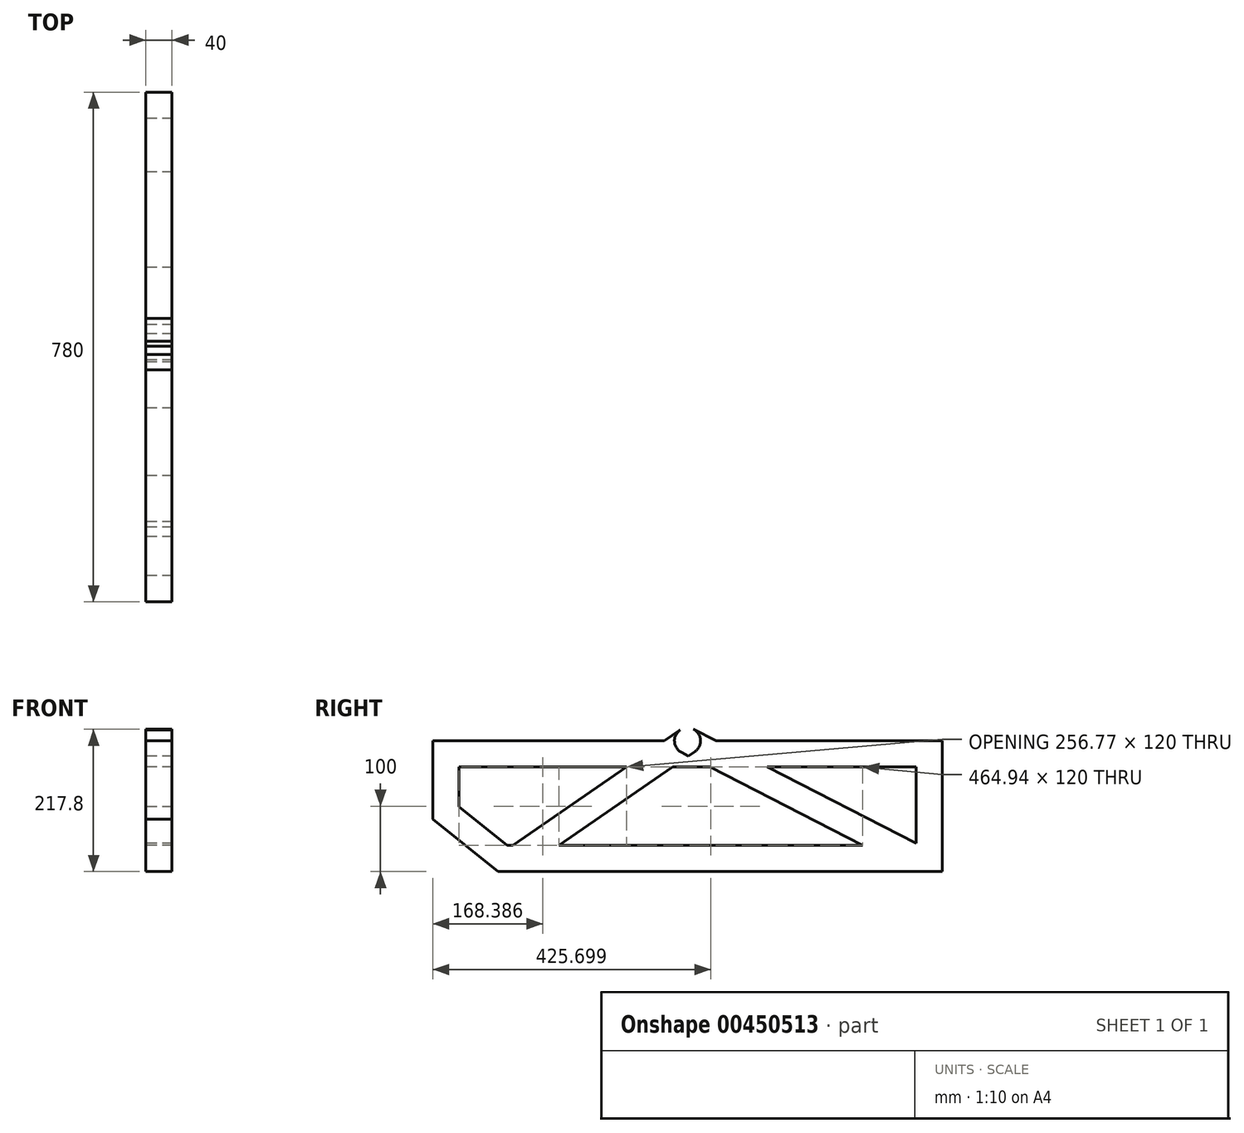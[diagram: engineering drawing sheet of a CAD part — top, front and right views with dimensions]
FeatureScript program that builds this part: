
annotation { "Feature Type Name" : "Feature", "Feature Type Description" : "" }
export const myFeature = defineFeature(function(context is Context, id is Id, definition is map)
    precondition{}
    {
        {
            var Q0;
            Q0=qCreatedBy(makeId("Right.planeOp"),FACE);
            var sketch = newSketch(context, id + "F0", { "sketchPlane" : qUnion([Q0])});
            skLineSegment(sketch, "E0", {"start": v(-369, 0) * mm, "end": v(-369, -20) * mm});
            skLineSegment(sketch, "E1", {"start": v(-369, -20) * mm, "end": v(-369, -100) * mm});
            skLineSegment(sketch, "E2", {"start": v(-369, -20) * mm, "end": v(-269, -20) * mm});
            skLineSegment(sketch, "E3", {"start": v(-369, -20) * mm, "end": v(-269, -100) * mm});
            skLineSegment(sketch, "E4", {"start": v(-269, -100) * mm, "end": v(411, -100) * mm});
            skLineSegment(sketch, "E5", {"start": v(411, -100) * mm, "end": v(411, 100) * mm});
            skLineSegment(sketch, "E6", {"start": v(411, 100) * mm, "end": v(-369, 100) * mm});
            skLineSegment(sketch, "E7", {"start": v(-369, 100) * mm, "end": v(-369, 0) * mm});
            skLineSegment(sketch, "E8", {"start": v(-269, -100) * mm, "end": v(21, 100) * mm});
            skLineSegment(sketch, "E9", {"start": v(21, 100) * mm, "end": v(411, -100) * mm});
            skLineSegment(sketch, "E10.0", {"start": v(-329, -0.78) * mm, "end": v(-254.97, -60) * mm});
            skLineSegment(sketch, "E10.1", {"start": v(-329, 60) * mm, "end": v(-329, -0.78) * mm});
            skLineSegment(sketch, "E10.2", {"start": v(-254.97, -60) * mm, "end": v(371, -60) * mm});
            skLineSegment(sketch, "E10.3", {"start": v(371, -60) * mm, "end": v(371, 60) * mm});
            skLineSegment(sketch, "E10.4", {"start": v(371, 60) * mm, "end": v(-329, 60) * mm});
            skArc(sketch, "E11.0.startCap", {"start": v(-257.65, -116.46) * mm, "mid": v(-285.46, -111.35) * mm, "end": v(-280.35, -83.54) * mm});
            skArc(sketch, "E11.0.endCap", {"start": v(9.65, 116.46) * mm, "mid": v(37.46, 111.35) * mm, "end": v(32.35, 83.54) * mm});
            skLineSegment(sketch, "E11.0.left", {"start": v(-280.35, -83.54) * mm, "end": v(9.65, 116.46) * mm});
            skLineSegment(sketch, "E11.0.right", {"start": v(-257.65, -116.46) * mm, "end": v(32.35, 83.54) * mm});
            skArc(sketch, "E11.1.startCap", {"start": v(11.87, 82.2) * mm, "mid": v(3.2, 109.13) * mm, "end": v(30.13, 117.8) * mm});
            skArc(sketch, "E11.1.endCap", {"start": v(420.13, -82.2) * mm, "mid": v(428.8, -109.13) * mm, "end": v(401.87, -117.8) * mm});
            skLineSegment(sketch, "E11.1.left", {"start": v(30.13, 117.8) * mm, "end": v(420.13, -82.2) * mm});
            skLineSegment(sketch, "E11.1.right", {"start": v(11.87, 82.2) * mm, "end": v(401.87, -117.8) * mm});
            skSolve(sketch);
        }
        {
            var Q0;
            {var subQ0=sQuery(id+"F0.wireOp",EDGE,"E10.2");var subQ1=sQuery(id+"F0.wireOp",EDGE,"E10.0");var subQ2=makeQuery(id+"F0.imprint","INTERSECT",VERTEX,{"derivedFrom":[subQ1,subQ0]});Q0=makeQuery(id+"F0.imprint","IMPRINT",FACE,{"disambiguationData":[TD([[makeQuery(id+"F0.imprint","IMPRINT",EDGE,{"disambiguationData":[TD([[subQ2,1.0]])],"derivedFrom":subQ1}),-1.0]])]});}
            var Q1;
            {var subQ0=sQuery(id+"F0.wireOp",EDGE,"E11.0.right");var subQ1=sQuery(id+"F0.wireOp",EDGE,"E4");var subQ2=makeQuery(id+"F0.imprint","INTERSECT",VERTEX,{"derivedFrom":[subQ1,subQ0]});Q1=makeQuery(id+"F0.imprint","IMPRINT",FACE,{"disambiguationData":[TD([[makeQuery(id+"F0.imprint","IMPRINT",EDGE,{"disambiguationData":[TD([[subQ2,-1.0]])],"derivedFrom":subQ1}),1.0]])]});}
            var Q2;
            {var subQ6=sQuery(id+"F0.wireOp",EDGE,"E6");var subQ7=sQuery(id+"F0.wireOp",EDGE,"E5");var subQ8=makeQuery(id+"F0.imprint","INTERSECT",VERTEX,{"derivedFrom":[subQ7,subQ6]});Q2=makeQuery(id+"F0.imprint","IMPRINT",FACE,{"disambiguationData":[TD([[makeQuery(id+"F0.imprint","IMPRINT",EDGE,{"disambiguationData":[TD([[subQ8,1.0]])],"derivedFrom":subQ7}),1.0]])]});}
            var Q3;
            {var subQ3=sQuery(id+"F0.wireOp",EDGE,"E11.1.left");var subQ7=sQuery(id+"F0.wireOp",EDGE,"E6");var subQ8=makeQuery(id+"F0.imprint","INTERSECT",VERTEX,{"derivedFrom":[subQ7,subQ3]});Q3=makeQuery(id+"F0.imprint","IMPRINT",FACE,{"disambiguationData":[TD([[makeQuery(id+"F0.imprint","IMPRINT",EDGE,{"disambiguationData":[TD([[subQ8,-1.0]])],"derivedFrom":subQ7}),1.0]])]});}
            var Q4;
            {var subQ1=sQuery(id+"F0.wireOp",EDGE,"E11.0.endCap");var subQ6=sQuery(id+"F0.wireOp",EDGE,"E9");var subQ9=makeQuery(id+"F0.imprint","INTERSECT",VERTEX,{"derivedFrom":[subQ6,subQ1]});Q4=makeQuery(id+"F0.imprint","IMPRINT",FACE,{"disambiguationData":[TD([[makeQuery(id+"F0.imprint","IMPRINT",EDGE,{"disambiguationData":[TD([[subQ9,-1.0]])],"derivedFrom":subQ6}),-1.0]])]});}
            var Q5;
            {var subQ0=sQuery(id+"F0.wireOp",EDGE,"E11.1.right");var subQ1=sQuery(id+"F0.wireOp",EDGE,"E10.4");var subQ2=makeQuery(id+"F0.imprint","INTERSECT",VERTEX,{"derivedFrom":[subQ1,subQ0]});Q5=makeQuery(id+"F0.imprint","IMPRINT",FACE,{"disambiguationData":[TD([[makeQuery(id+"F0.imprint","IMPRINT",EDGE,{"disambiguationData":[TD([[subQ2,-1.0]])],"derivedFrom":subQ1}),-1.0]])]});}
            var Q6;
            {var subQ3=sQuery(id+"F0.wireOp",EDGE,"E8");var subQ6=sQuery(id+"F0.wireOp",EDGE,"E10.4");var subQ9=makeQuery(id+"F0.imprint","INTERSECT",VERTEX,{"derivedFrom":[subQ3,subQ6]});Q6=makeQuery(id+"F0.imprint","IMPRINT",FACE,{"disambiguationData":[TD([[makeQuery(id+"F0.imprint","IMPRINT",EDGE,{"disambiguationData":[TD([[subQ9,-1.0]])],"derivedFrom":subQ3}),-1.0]])]});}
            var Q7;
            {var subQ0=sQuery(id+"F0.wireOp",EDGE,"E11.0.left");var subQ1=sQuery(id+"F0.wireOp",EDGE,"E6");var subQ2=makeQuery(id+"F0.imprint","INTERSECT",VERTEX,{"derivedFrom":[subQ1,subQ0]});Q7=makeQuery(id+"F0.imprint","IMPRINT",FACE,{"disambiguationData":[TD([[makeQuery(id+"F0.imprint","IMPRINT",EDGE,{"disambiguationData":[TD([[subQ2,1.0]])],"derivedFrom":subQ1}),1.0]])]});}
            var Q8;
            {var subQ1=sQuery(id+"F0.wireOp",EDGE,"E6");var subQ3=sQuery(id+"F0.wireOp",EDGE,"E11.1.startCap");var subQ4=makeQuery(id+"F0.imprint","INTERSECT",VERTEX,{"derivedFrom":[subQ1,subQ3]});Q8=makeQuery(id+"F0.imprint","IMPRINT",FACE,{"disambiguationData":[TD([[makeQuery(id+"F0.imprint","IMPRINT",EDGE,{"disambiguationData":[TD([[subQ4,1.0]])],"derivedFrom":subQ3}),-1.0]])]});}
            var Q9;
            {var subQ0=sQuery(id+"F0.wireOp",EDGE,"E11.0.right");var subQ1=sQuery(id+"F0.wireOp",EDGE,"E11.0.endCap");var subQ2=makeQuery(id+"F0.imprint","INTERSECT",VERTEX,{"derivedFrom":[subQ1,subQ0]});Q9=makeQuery(id+"F0.imprint","IMPRINT",FACE,{"disambiguationData":[TD([[makeQuery(id+"F0.imprint","IMPRINT",EDGE,{"disambiguationData":[TD([[subQ2,1.0]])],"derivedFrom":subQ1}),-1.0]])]});}
            var Q10;
            {var subQ1=sQuery(id+"F0.wireOp",EDGE,"E6");var subQ3=sQuery(id+"F0.wireOp",EDGE,"E11.0.endCap");var subQ4=makeQuery(id+"F0.imprint","INTERSECT",VERTEX,{"derivedFrom":[subQ1,subQ3]});Q10=makeQuery(id+"F0.imprint","IMPRINT",FACE,{"disambiguationData":[TD([[makeQuery(id+"F0.imprint","IMPRINT",EDGE,{"disambiguationData":[TD([[subQ4,-1.0]])],"derivedFrom":subQ3}),-1.0]])]});}
            var Q11;
            {var subQ5=sQuery(id+"F0.wireOp",EDGE,"E0");Q11=makeQuery(id+"F0.imprint","IMPRINT",FACE,{"disambiguationData":[TD([[makeQuery(id+"F0.imprint","IMPRINT",EDGE,{"derivedFrom":subQ5}),1.0]])]});}
            var Q12;
            {var subQ0=sQuery(id+"F0.wireOp",EDGE,"E8");var subQ5=sQuery(id+"F0.wireOp",EDGE,"E10.2");var subQ6=makeQuery(id+"F0.imprint","INTERSECT",VERTEX,{"derivedFrom":[subQ0,subQ5]});Q12=makeQuery(id+"F0.imprint","IMPRINT",FACE,{"disambiguationData":[TD([[makeQuery(id+"F0.imprint","IMPRINT",EDGE,{"disambiguationData":[TD([[subQ6,-1.0]])],"derivedFrom":subQ5}),-1.0]])]});}
            var Q13;
            {var subQ0=sQuery(id+"F0.wireOp",EDGE,"E8");var subQ3=sQuery(id+"F0.wireOp",EDGE,"E10.2");var subQ4=makeQuery(id+"F0.imprint","INTERSECT",VERTEX,{"derivedFrom":[subQ0,subQ3]});Q13=makeQuery(id+"F0.imprint","IMPRINT",FACE,{"disambiguationData":[TD([[makeQuery(id+"F0.imprint","IMPRINT",EDGE,{"disambiguationData":[TD([[subQ4,1.0]])],"derivedFrom":subQ3}),-1.0]])]});}
            var Q14;
            {var subQ0=sQuery(id+"F0.wireOp",EDGE,"E10.2");var subQ1=sQuery(id+"F0.wireOp",EDGE,"E8");var subQ2=makeQuery(id+"F0.imprint","INTERSECT",VERTEX,{"derivedFrom":[subQ1,subQ0]});Q14=makeQuery(id+"F0.imprint","IMPRINT",FACE,{"disambiguationData":[TD([[makeQuery(id+"F0.imprint","IMPRINT",EDGE,{"disambiguationData":[TD([[subQ2,-1.0]])],"derivedFrom":subQ1}),1.0]])]});}
            var Q15;
            {var subQ0=sQuery(id+"F0.wireOp",EDGE,"E10.2");var subQ1=sQuery(id+"F0.wireOp",EDGE,"E8");var subQ2=makeQuery(id+"F0.imprint","INTERSECT",VERTEX,{"derivedFrom":[subQ1,subQ0]});Q15=makeQuery(id+"F0.imprint","IMPRINT",FACE,{"disambiguationData":[TD([[makeQuery(id+"F0.imprint","IMPRINT",EDGE,{"disambiguationData":[TD([[subQ2,-1.0]])],"derivedFrom":subQ1}),-1.0]])]});}
            var Q16;
            {var subQ0=sQuery(id+"F0.wireOp",EDGE,"E10.4");var subQ1=sQuery(id+"F0.wireOp",EDGE,"E9");var subQ2=makeQuery(id+"F0.imprint","INTERSECT",VERTEX,{"derivedFrom":[subQ1,subQ0]});Q16=makeQuery(id+"F0.imprint","IMPRINT",FACE,{"disambiguationData":[TD([[makeQuery(id+"F0.imprint","IMPRINT",EDGE,{"disambiguationData":[TD([[subQ2,-1.0]])],"derivedFrom":subQ1}),-1.0]])]});}
            var Q17;
            {var subQ0=sQuery(id+"F0.wireOp",EDGE,"E10.4");var subQ1=sQuery(id+"F0.wireOp",EDGE,"E9");var subQ2=makeQuery(id+"F0.imprint","INTERSECT",VERTEX,{"derivedFrom":[subQ1,subQ0]});Q17=makeQuery(id+"F0.imprint","IMPRINT",FACE,{"disambiguationData":[TD([[makeQuery(id+"F0.imprint","IMPRINT",EDGE,{"disambiguationData":[TD([[subQ2,-1.0]])],"derivedFrom":subQ1}),1.0]])]});}
            var Q18;
            {var subQ0=sQuery(id+"F0.wireOp",EDGE,"E9");var subQ5=sQuery(id+"F0.wireOp",EDGE,"E10.2");var subQ6=makeQuery(id+"F0.imprint","INTERSECT",VERTEX,{"derivedFrom":[subQ0,subQ5]});Q18=makeQuery(id+"F0.imprint","IMPRINT",FACE,{"disambiguationData":[TD([[makeQuery(id+"F0.imprint","IMPRINT",EDGE,{"disambiguationData":[TD([[subQ6,1.0]])],"derivedFrom":subQ5}),-1.0]])]});}
            var Q19;
            {var subQ0=sQuery(id+"F0.wireOp",EDGE,"E10.3");var subQ1=sQuery(id+"F0.wireOp",EDGE,"E10.2");var subQ2=makeQuery(id+"F0.imprint","INTERSECT",VERTEX,{"derivedFrom":[subQ1,subQ0]});Q19=makeQuery(id+"F0.imprint","IMPRINT",FACE,{"disambiguationData":[TD([[makeQuery(id+"F0.imprint","IMPRINT",EDGE,{"disambiguationData":[TD([[subQ2,1.0]])],"derivedFrom":subQ1}),-1.0]])]});}
            extrude(context, id + "F1", {"entities" : qUnion([Q0, Q1, Q2, Q3, Q4, Q5, Q6, Q7, Q8, Q9, Q10, Q11, Q12, Q13, Q14, Q15, Q16, Q17, Q18, Q19]), "endBound" : BoundingType.SYMMETRIC, "depth" : 40 * mm});
        }
    });
